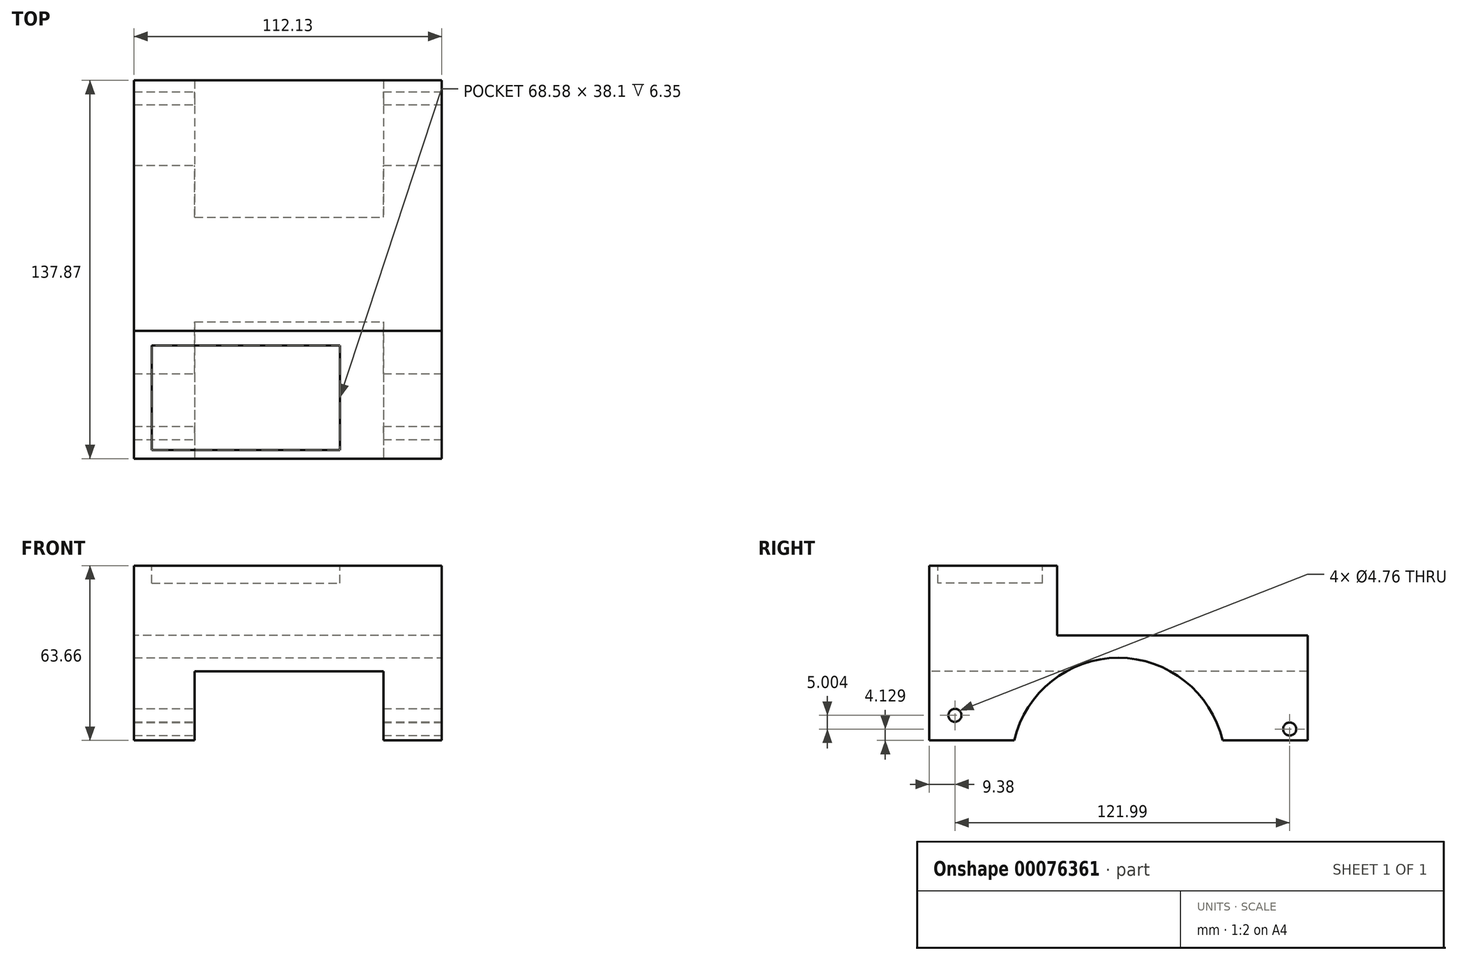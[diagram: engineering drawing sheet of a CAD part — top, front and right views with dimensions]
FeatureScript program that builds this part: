
annotation { "Feature Type Name" : "Feature", "Feature Type Description" : "" }
export const myFeature = defineFeature(function(context is Context, id is Id, definition is map)
    precondition{}
    {
        {
            var Q0;
            Q0=qCreatedBy(makeId("Front.planeOp"),FACE);
            var sketch = newSketch(context, id + "F0", { "sketchPlane" : qUnion([Q0])});
            skLineSegment(sketch, "E0.bottom", {"start": v(-57.39, 38.26) * mm, "end": v(54.74, 38.26) * mm});
            skLineSegment(sketch, "E0.top", {"start": v(-57.39, 0) * mm, "end": v(54.74, 0) * mm});
            skLineSegment(sketch, "E0.left", {"start": v(-57.39, 38.26) * mm, "end": v(-57.39, 0) * mm});
            skLineSegment(sketch, "E0.right", {"start": v(54.74, 38.26) * mm, "end": v(54.74, 0) * mm});
            skSolve(sketch);
        }
        {
            var Q0;
            Q0=makeQuery(id+"F0.imprint","IMPRINT",FACE,{"disambiguationData":[TD([[makeQuery(id+"F0.imprint","IMPRINT",EDGE,{"derivedFrom":sQuery(id+"F0.wireOp",EDGE,"E0.bottom")}),-1.0]])]});
            extrude(context, id + "F1", {"entities" : qUnion([Q0]), "depth" : 137.87 * mm});
        }
        {
            var Q0;
            Q0=makeQuery(id+"F1.opExtrude","CAP_FACE",FACE,{"disambiguationData":[OSD([sQuery(id+"F0.wireOp",EDGE,"E0.bottom"),sQuery(id+"F0.wireOp",EDGE,"E0.top"),sQuery(id+"F0.wireOp",EDGE,"E0.left"),sQuery(id+"F0.wireOp",EDGE,"E0.right")])],"isStart":false});
            var sketch = newSketch(context, id + "F2", { "sketchPlane" : qUnion([Q0])});
            skLineSegment(sketch, "E1.bottom", {"start": v(-35.27, 25.15) * mm, "end": v(33.51, 25.15) * mm});
            skLineSegment(sketch, "E1.top", {"start": v(-35.27, 0) * mm, "end": v(33.51, 0) * mm});
            skLineSegment(sketch, "E1.left", {"start": v(-35.27, 25.15) * mm, "end": v(-35.27, 0) * mm});
            skLineSegment(sketch, "E1.right", {"start": v(33.51, 25.15) * mm, "end": v(33.51, 0) * mm});
            skSolve(sketch);
        }
        {
            var Q0;
            Q0=makeQuery(id+"F2.imprint","IMPRINT",FACE,{"disambiguationData":[TD([[makeQuery(id+"F2.imprint","IMPRINT",EDGE,{"derivedFrom":sQuery(id+"F2.wireOp",EDGE,"E1.bottom")}),-1.0]])]});
            extrude(context, id + "F3", {"entities" : qUnion([Q0]), "operationType" : NewBodyOperationType.REMOVE, "endBound" : BoundingType.THROUGH_ALL, "oppositeDirection" : true, "depth" : 25.4 * mm});
        }
        {
            var Q0;
            Q0=makeQuery(id+"F1.opExtrude","SWEPT_FACE",FACE,{"disambiguationData":[OSD([sQuery(id+"F0.wireOp",EDGE,"E0.right")])]});
            var sketch = newSketch(context, id + "F4", { "sketchPlane" : qUnion([Q0])});
            skCircle(sketch, "E2", {"center": v(-128.5, 9.13) * mm, "radius": 2.38 * mm});
            skSolve(sketch);
        }
        {
            var Q0;
            Q0=makeQuery(id+"F4.imprint","IMPRINT",FACE,{"disambiguationData":[TD([[makeQuery(id+"F4.imprint","IMPRINT",EDGE,{"derivedFrom":sQuery(id+"F4.wireOp",EDGE,"E2")}),1.0]])]});
            extrude(context, id + "F5", {"entities" : qUnion([Q0]), "operationType" : NewBodyOperationType.REMOVE, "endBound" : BoundingType.THROUGH_ALL, "oppositeDirection" : true, "depth" : 25.4 * mm});
        }
        {
            var Q0;
            Q0=makeQuery(id+"F1.opExtrude","SWEPT_FACE",FACE,{"disambiguationData":[OSD([sQuery(id+"F0.wireOp",EDGE,"E0.right")])]});
            var sketch = newSketch(context, id + "F6", { "sketchPlane" : qUnion([Q0])});
            skCircle(sketch, "E3", {"center": v(-6.5, 4.13) * mm, "radius": 2.38 * mm});
            skSolve(sketch);
        }
        {
            var Q0;
            Q0=makeQuery(id+"F6.imprint","IMPRINT",FACE,{"disambiguationData":[TD([[makeQuery(id+"F6.imprint","IMPRINT",EDGE,{"derivedFrom":sQuery(id+"F6.wireOp",EDGE,"E3")}),1.0]])]});
            extrude(context, id + "F7", {"entities" : qUnion([Q0]), "operationType" : NewBodyOperationType.REMOVE, "endBound" : BoundingType.THROUGH_ALL, "oppositeDirection" : true, "depth" : 25.4 * mm});
        }
        {
            var Q0;
            Q0=makeQuery(id+"F1.opExtrude","SWEPT_FACE",FACE,{"disambiguationData":[OSD([sQuery(id+"F0.wireOp",EDGE,"E0.right")])]});
            var sketch = newSketch(context, id + "F8", { "sketchPlane" : qUnion([Q0])});
            skCircle(sketch, "E4", {"center": v(-68.94, -8.9) * mm, "radius": 39 * mm});
            skPoint(sketch, "E4.centerSnap0", {"position": v(-68.94, 0) * mm});
            skSolve(sketch);
        }
        {
            var Q0;
            {var subQ0=sQuery(id+"F8.wireOp",EDGE,"E4");var subQ1=makeQuery(id+"F1.opExtrude","SWEPT_EDGE",EDGE,{"disambiguationData":[OSD([sQuery(id+"F0.wireOp",EDGE,"E0.top"),sQuery(id+"F0.wireOp",EDGE,"E0.right")])]});var subQ2=makeQuery(id+"F8.imprint","INTERSECT",VERTEX,{"disambiguationData":[OD(0.0)],"derivedFrom":[subQ1,subQ0]});Q0=makeQuery(id+"F8.imprint","IMPRINT",FACE,{"disambiguationData":[TD([[makeQuery(id+"F8.imprint","IMPRINT",EDGE,{"disambiguationData":[TD([[subQ2,-1.0]])],"derivedFrom":subQ0}),1.0]])]});}
            extrude(context, id + "F9", {"entities" : qUnion([Q0]), "operationType" : NewBodyOperationType.REMOVE, "endBound" : BoundingType.THROUGH_ALL, "oppositeDirection" : true, "depth" : 25.4 * mm});
        }
        {
            var Q0;
            Q0=makeQuery(id+"F1.opExtrude","SWEPT_FACE",FACE,{"disambiguationData":[OSD([sQuery(id+"F0.wireOp",EDGE,"E0.bottom")])]});
            var sketch = newSketch(context, id + "F10", { "sketchPlane" : qUnion([Q0])});
            skLineSegment(sketch, "E5", {"start": v(0, -91.25) * mm, "end": v(-57.39, -91.25) * mm});
            skLineSegment(sketch, "E6", {"start": v(-57.39, -91.25) * mm, "end": v(-57.39, -137.87) * mm});
            skLineSegment(sketch, "E7", {"start": v(-57.39, -137.87) * mm, "end": v(54.74, -137.87) * mm});
            skLineSegment(sketch, "E8", {"start": v(54.74, -137.87) * mm, "end": v(54.74, -91.25) * mm});
            skLineSegment(sketch, "E9", {"start": v(54.74, -91.25) * mm, "end": v(0, -91.25) * mm});
            skSolve(sketch);
        }
        {
            var Q0;
            Q0=makeQuery(id+"F10.imprint","IMPRINT",FACE,{"disambiguationData":[TD([[makeQuery(id+"F10.imprint","IMPRINT",EDGE,{"derivedFrom":sQuery(id+"F10.wireOp",EDGE,"E5")}),1.0]])]});
            extrude(context, id + "F11", {"entities" : qUnion([Q0]), "operationType" : NewBodyOperationType.ADD, "depth" : 25.4 * mm});
        }
        {
            var Q0;
            Q0=makeQuery(id+"F11.opExtrude","CAP_FACE",FACE,{"disambiguationData":[OSD([sQuery(id+"F10.wireOp",EDGE,"E5"),sQuery(id+"F10.wireOp",EDGE,"E6"),sQuery(id+"F10.wireOp",EDGE,"E7"),sQuery(id+"F10.wireOp",EDGE,"E8"),sQuery(id+"F10.wireOp",EDGE,"E9")])],"isStart":false});
            var sketch = newSketch(context, id + "F12", { "sketchPlane" : qUnion([Q0])});
            skLineSegment(sketch, "E10.bottom", {"start": v(-50.91, -96.56) * mm, "end": v(17.67, -96.56) * mm});
            skLineSegment(sketch, "E10.top", {"start": v(-50.91, -134.66) * mm, "end": v(17.67, -134.66) * mm});
            skLineSegment(sketch, "E10.left", {"start": v(-50.91, -96.56) * mm, "end": v(-50.91, -134.66) * mm});
            skLineSegment(sketch, "E10.right", {"start": v(17.67, -96.56) * mm, "end": v(17.67, -134.66) * mm});
            skSolve(sketch);
        }
        {
            var Q0;
            Q0=makeQuery(id+"F12.imprint","IMPRINT",FACE,{"disambiguationData":[TD([[makeQuery(id+"F12.imprint","IMPRINT",EDGE,{"derivedFrom":sQuery(id+"F12.wireOp",EDGE,"E10.bottom")}),-1.0]])]});
            extrude(context, id + "F13", {"entities" : qUnion([Q0]), "operationType" : NewBodyOperationType.REMOVE, "oppositeDirection" : true, "depth" : 6.35 * mm});
        }
    });
